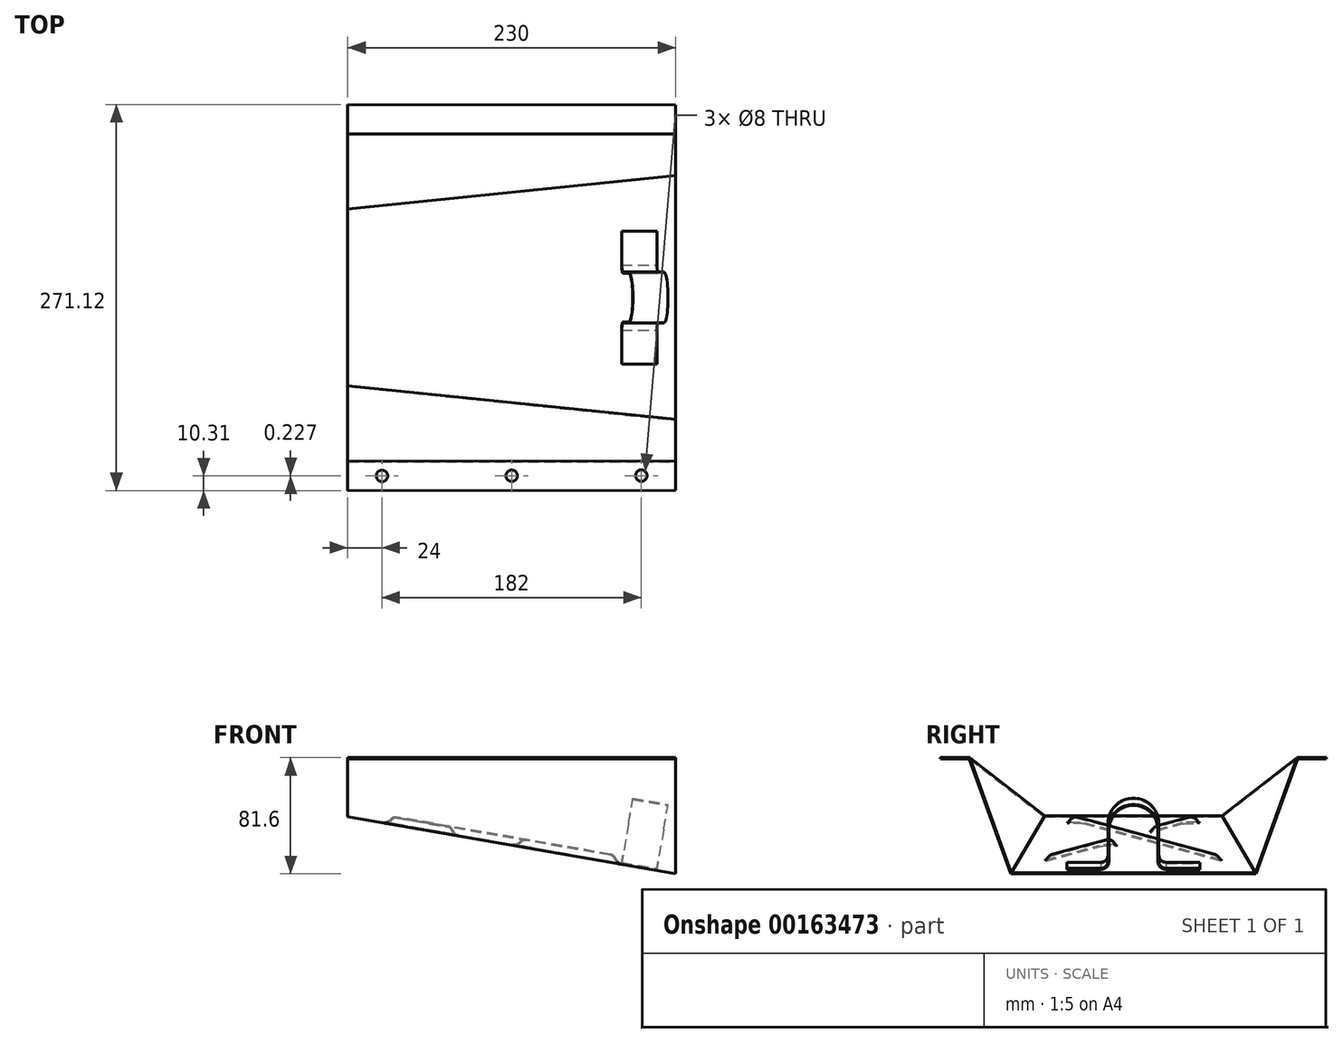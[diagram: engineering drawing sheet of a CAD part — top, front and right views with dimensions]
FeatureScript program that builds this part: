
annotation { "Feature Type Name" : "Feature", "Feature Type Description" : "" }
export const myFeature = defineFeature(function(context is Context, id is Id, definition is map)
    precondition{}
    {
        {
            var Q0;
            Q0=qCreatedBy(makeId("Right.planeOp"),FACE);
            var sketch = newSketch(context, id + "F0", { "sketchPlane" : qUnion([Q0])});
            skLineSegment(sketch, "E0", {"start": v(-135.27, 0) * mm, "end": v(135.27, 0) * mm, "construction": true});
            skLineSegment(sketch, "E1", {"start": v(0, 69.22) * mm, "end": v(0, -69.22) * mm, "construction": true});
            skLineSegment(sketch, "E2", {"start": v(-135.27, 0) * mm, "end": v(-115.27, 0) * mm});
            skLineSegment(sketch, "E3", {"start": v(-115.27, 0) * mm, "end": v(-62.4, -40.8) * mm});
            skLineSegment(sketch, "E4", {"start": v(-62.4, -40.8) * mm, "end": v(0, -40.8) * mm});
            skLineSegment(sketch, "E5.MirrorCS", {"start": v(62.4, -40.8) * mm, "end": v(0, -40.8) * mm});
            skLineSegment(sketch, "E6.MirrorCS", {"start": v(115.27, 0) * mm, "end": v(62.4, -40.8) * mm});
            skLineSegment(sketch, "E7.MirrorCS", {"start": v(135.27, 0) * mm, "end": v(115.27, 0) * mm});
            skLineSegment(sketch, "E8.0", {"start": v(135.56, 0.8) * mm, "end": v(115, 0.8) * mm});
            skLineSegment(sketch, "E8.1", {"start": v(115, 0.8) * mm, "end": v(62.13, -40) * mm});
            skLineSegment(sketch, "E8.2", {"start": v(-135.56, 0.8) * mm, "end": v(-115, 0.8) * mm});
            skLineSegment(sketch, "E8.3", {"start": v(-115, 0.8) * mm, "end": v(-62.13, -40) * mm});
            skLineSegment(sketch, "E8.4", {"start": v(-62.13, -40) * mm, "end": v(0, -40) * mm});
            skLineSegment(sketch, "E8.5", {"start": v(62.13, -40) * mm, "end": v(0, -40) * mm});
            skLineSegment(sketch, "E9", {"start": v(-135.56, 0.8) * mm, "end": v(-135.27, 0) * mm});
            skLineSegment(sketch, "E10", {"start": v(135.56, 0.8) * mm, "end": v(135.27, 0) * mm});
            skSolve(sketch);
        }
        {
            var Q0;
            Q0=qCreatedBy(makeId("Right.planeOp"),FACE);
            cPlane(context, id + "F1", {"entities" : qUnion([Q0]), "cplaneType" : CPlaneType.OFFSET, "offset" : 230 * mm, "width" : 150 * mm, "height" : 150 * mm});
        }
        {
            var Q0;
            Q0=qCreatedBy(id+"F1.planeOp",FACE);
            var sketch = newSketch(context, id + "F2", { "sketchPlane" : qUnion([Q0])});
            skLineSegment(sketch, "E11", {"start": v(-135.27, 0) * mm, "end": v(-115.27, 0) * mm});
            skLineSegment(sketch, "E12", {"start": v(-115.27, 0) * mm, "end": v(-86.15, -80.8) * mm});
            skLineSegment(sketch, "E13", {"start": v(-86.15, -80.8) * mm, "end": v(0, -80.8) * mm});
            skLineSegment(sketch, "E14.MirrorCS", {"start": v(86.15, -80.8) * mm, "end": v(0, -80.8) * mm});
            skLineSegment(sketch, "E15.MirrorCS", {"start": v(115.27, 0) * mm, "end": v(86.15, -80.8) * mm});
            skLineSegment(sketch, "E16.MirrorCS", {"start": v(135.27, 0) * mm, "end": v(115.27, 0) * mm});
            skLineSegment(sketch, "E17.0", {"start": v(135.27, 0.8) * mm, "end": v(114.71, 0.8) * mm});
            skLineSegment(sketch, "E17.1", {"start": v(114.71, 0.8) * mm, "end": v(85.6, -80) * mm});
            skLineSegment(sketch, "E17.2", {"start": v(-135.27, 0.8) * mm, "end": v(-114.71, 0.8) * mm});
            skLineSegment(sketch, "E17.3", {"start": v(-114.71, 0.8) * mm, "end": v(-85.6, -80) * mm});
            skLineSegment(sketch, "E17.4", {"start": v(-85.6, -80) * mm, "end": v(-8.72, -80) * mm});
            skLineSegment(sketch, "E17.5", {"start": v(85.6, -80) * mm, "end": v(-8.72, -80) * mm});
            skLineSegment(sketch, "E18", {"start": v(135.27, 0.8) * mm, "end": v(135.27, 0) * mm});
            skLineSegment(sketch, "E19", {"start": v(-135.27, 0.8) * mm, "end": v(-135.27, 0) * mm});
            skSolve(sketch);
        }
        {
            var Q0;
            Q0=makeQuery(id+"F0.imprint","IMPRINT",FACE,{"disambiguationData":[TD([[makeQuery(id+"F0.imprint","IMPRINT",EDGE,{"derivedFrom":sQuery(id+"F0.wireOp",EDGE,"E2")}),1.0]])]});
            var Q1;
            Q1=makeQuery(id+"F2.imprint","IMPRINT",FACE,{"disambiguationData":[TD([[makeQuery(id+"F2.imprint","IMPRINT",EDGE,{"derivedFrom":sQuery(id+"F2.wireOp",EDGE,"E11")}),1.0]])]});
            loft(context, id + "F3", {"sheetProfilesArray" : [{ "sheetProfileEntities" : qUnion([Q0]) }, { "sheetProfileEntities" : qUnion([Q1]) }]});
        }
        {
            var Q0;
            Q0=makeQuery(id+"F3.opLoft","SWEPT_FACE",FACE,{"disambiguationData":[OSD([sQuery(id+"F0.wireOp",EDGE,"E8.1"),sQuery(id+"F0.wireOp",EDGE,"E8.4"),sQuery(id+"F0.wireOp",EDGE,"E8.5"),sQuery(id+"F2.wireOp",EDGE,"E17.1"),sQuery(id+"F2.wireOp",EDGE,"E17.4"),sQuery(id+"F2.wireOp",EDGE,"E17.5")])]});
            var sketch = newSketch(context, id + "F4", { "sketchPlane" : qUnion([Q0])});
            skLineSegment(sketch, "E20", {"start": v(6.85, -62.13) * mm, "end": v(240.3, 85.6) * mm, "construction": true});
            skLineSegment(sketch, "E21", {"start": v(240.3, -85.6) * mm, "end": v(6.85, 62.13) * mm, "construction": true});
            skArc(sketch, "E22", {"start": v(38.45, -36.22) * mm, "mid": v(36.9, -43.12) * mm, "end": v(43.8, -44.67) * mm});
            skArc(sketch, "E23", {"start": v(195.77, 51.5) * mm, "mid": v(197.32, 58.4) * mm, "end": v(190.42, 59.95) * mm});
            skLineSegment(sketch, "E24", {"start": v(195.77, 51.5) * mm, "end": v(43.8, -44.67) * mm});
            skLineSegment(sketch, "E25", {"start": v(38.45, -36.22) * mm, "end": v(190.42, 59.95) * mm});
            skArc(sketch, "E26", {"start": v(43.8, 44.67) * mm, "mid": v(36.9, 43.12) * mm, "end": v(38.45, 36.22) * mm});
            skArc(sketch, "E27", {"start": v(74.31, 13.53) * mm, "mid": v(81.21, 15.08) * mm, "end": v(79.66, 21.98) * mm});
            skArc(sketch, "E28", {"start": v(190.42, -59.95) * mm, "mid": v(197.32, -58.4) * mm, "end": v(195.77, -51.5) * mm});
            skArc(sketch, "E29", {"start": v(135.76, -13.53) * mm, "mid": v(128.87, -15.08) * mm, "end": v(130.42, -21.98) * mm});
            skLineSegment(sketch, "E30", {"start": v(195.77, -51.5) * mm, "end": v(135.76, -13.53) * mm});
            skLineSegment(sketch, "E31", {"start": v(190.42, -59.95) * mm, "end": v(130.42, -21.98) * mm});
            skLineSegment(sketch, "E32", {"start": v(43.8, 44.67) * mm, "end": v(79.66, 21.98) * mm});
            skLineSegment(sketch, "E33", {"start": v(38.45, 36.22) * mm, "end": v(74.31, 13.53) * mm});
            skLineSegment(sketch, "E34.0", {"start": v(195.34, -52.17) * mm, "end": v(135.34, -14.2) * mm});
            skArc(sketch, "E34.1", {"start": v(190.85, -59.27) * mm, "mid": v(196.65, -57.97) * mm, "end": v(195.34, -52.17) * mm});
            skLineSegment(sketch, "E34.2", {"start": v(190.85, -59.27) * mm, "end": v(130.85, -21.3) * mm});
            skArc(sketch, "E34.3", {"start": v(135.34, -14.2) * mm, "mid": v(129.54, -15.5) * mm, "end": v(130.85, -21.3) * mm});
            skLineSegment(sketch, "E35", {"start": v(226.93, -41.34) * mm, "end": v(226.93, 41.34) * mm, "construction": true});
            skLineSegment(sketch, "E36", {"start": v(168.2, 0) * mm, "end": v(226.93, 0) * mm, "construction": true});
            skSolve(sketch);
        }
        {
            var Q0;
            Q0=makeQuery(id+"F4.imprint","IMPRINT",FACE,{"disambiguationData":[TD([[makeQuery(id+"F4.imprint","IMPRINT",EDGE,{"derivedFrom":sQuery(id+"F4.wireOp",EDGE,"E28")}),1.0]])]});
            var Q1;
            Q1=makeQuery(id+"F4.imprint","IMPRINT",FACE,{"disambiguationData":[TD([[makeQuery(id+"F4.imprint","IMPRINT",EDGE,{"derivedFrom":sQuery(id+"F4.wireOp",EDGE,"E22")}),1.0]])]});
            var Q2;
            Q2=makeQuery(id+"F4.imprint","IMPRINT",FACE,{"disambiguationData":[TD([[makeQuery(id+"F4.imprint","IMPRINT",EDGE,{"derivedFrom":sQuery(id+"F4.wireOp",EDGE,"E26")}),1.0]])]});
            var Q3;
            Q3=makeQuery(id+"F4.imprint","IMPRINT",FACE,{"disambiguationData":[TD([[makeQuery(id+"F4.imprint","IMPRINT",EDGE,{"derivedFrom":sQuery(id+"F4.wireOp",EDGE,"E34.0")}),1.0]])]});
            extrude(context, id + "F5", {"entities" : qUnion([Q0, Q1, Q2, Q3]), "operationType" : NewBodyOperationType.ADD, "depth" : 5 * mm});
        }
        {
            var Q0;
            Q0=makeQuery(id+"F5.opExtrude","CAP_EDGE",EDGE,{"disambiguationData":[OSD([sQuery(id+"F4.wireOp",EDGE,"E30")])],"isStart":false});
            var Q1;
            Q1=makeQuery(id+"F5.opExtrude","CAP_EDGE",EDGE,{"disambiguationData":[OSD([sQuery(id+"F4.wireOp",EDGE,"E24")])],"isStart":false});
            var Q2;
            Q2=makeQuery(id+"F5.opExtrude","CAP_EDGE",EDGE,{"disambiguationData":[OSD([sQuery(id+"F4.wireOp",EDGE,"E27")])],"isStart":false});
            fillet(context, id + "F6", {"entities" : qUnion([Q0, Q1, Q2]), "radius" : 5 * mm, "tangentPropagation" : true, "allowEdgeOverflow" : false});
        }
        {
            var Q0;
            Q0=makeQuery(id+"F3.opLoft","SWEPT_FACE",FACE,{"disambiguationData":[OSD([sQuery(id+"F0.wireOp",EDGE,"E3"),sQuery(id+"F0.wireOp",EDGE,"E4"),sQuery(id+"F0.wireOp",EDGE,"E5.MirrorCS"),sQuery(id+"F2.wireOp",EDGE,"E12"),sQuery(id+"F2.wireOp",EDGE,"E13"),sQuery(id+"F2.wireOp",EDGE,"E14.MirrorCS")])]});
            shell(context, id + "F7", {"entities" : qUnion([Q0]), "thickness" : 0.8 * mm});
        }
        {
            var Q0;
            Q0=sQuery(id+"F4.wireOp",VERTEX,"E36.end");
            var Q1;
            Q1=sQuery(id+"F4.wireOp",EDGE,"E36");
            cPlane(context, id + "F8", {"entities" : qUnion([Q0, Q1]), "cplaneType" : CPlaneType.LINE_POINT, "offset" : 25 * mm, "width" : 150 * mm, "height" : 150 * mm});
        }
        {
            var Q0;
            Q0=qCreatedBy(id+"F8.planeOp",FACE);
            var sketch = newSketch(context, id + "F9", { "sketchPlane" : qUnion([Q0])});
            skArc(sketch, "E37", {"start": v(17.92, -10.95) * mm, "mid": v(0, 6.97) * mm, "end": v(-17.92, -10.95) * mm});
            skLineSegment(sketch, "E38", {"start": v(-17.92, -10.95) * mm, "end": v(-17.92, -33.6) * mm});
            skLineSegment(sketch, "E39", {"start": v(-22.92, -38.6) * mm, "end": v(-46.63, -38.6) * mm});
            skLineSegment(sketch, "E40.MirrorCS", {"start": v(17.92, -10.95) * mm, "end": v(17.92, -33.6) * mm});
            skLineSegment(sketch, "E41.MirrorCS", {"start": v(22.92, -38.6) * mm, "end": v(46.63, -38.6) * mm});
            skPoint(sketch, "E42.visualSharp", {"position": v(-17.92, -38.6) * mm});
            skArc(sketch, "E42.filletArc", {"start": v(-22.92, -38.6) * mm, "mid": v(-19.39, -37.14) * mm, "end": v(-17.92, -33.6) * mm});
            skPoint(sketch, "E43.visualSharp", {"position": v(17.92, -38.6) * mm});
            skArc(sketch, "E43.filletArc", {"start": v(17.92, -33.6) * mm, "mid": v(19.39, -37.14) * mm, "end": v(22.92, -38.6) * mm});
            skLineSegment(sketch, "E44.0", {"start": v(22.92, -39.4) * mm, "end": v(46.63, -39.4) * mm});
            skArc(sketch, "E44.1", {"start": v(17.12, -33.6) * mm, "mid": v(18.82, -37.7) * mm, "end": v(22.92, -39.4) * mm});
            skLineSegment(sketch, "E44.2", {"start": v(17.12, -10.95) * mm, "end": v(17.12, -33.6) * mm});
            skLineSegment(sketch, "E44.3", {"start": v(-22.92, -39.4) * mm, "end": v(-46.63, -39.4) * mm});
            skArc(sketch, "E44.4", {"start": v(-22.92, -39.4) * mm, "mid": v(-18.82, -37.7) * mm, "end": v(-17.12, -33.6) * mm});
            skLineSegment(sketch, "E44.5", {"start": v(-17.12, -10.95) * mm, "end": v(-17.12, -33.6) * mm});
            skArc(sketch, "E44.6", {"start": v(17.12, -10.95) * mm, "mid": v(0, 6.17) * mm, "end": v(-17.12, -10.95) * mm});
            skLineSegment(sketch, "E45", {"start": v(46.63, -38.6) * mm, "end": v(46.63, -39.4) * mm});
            skLineSegment(sketch, "E46", {"start": v(-46.63, -38.6) * mm, "end": v(-46.63, -39.4) * mm});
            skSolve(sketch);
        }
        {
            var Q0;
            Q0=makeQuery(id+"F9.imprint","IMPRINT",FACE,{"disambiguationData":[TD([[makeQuery(id+"F9.imprint","IMPRINT",EDGE,{"derivedFrom":sQuery(id+"F9.wireOp",EDGE,"E37")}),1.0]])]});
            extrude(context, id + "F10", {"entities" : qUnion([Q0]), "operationType" : NewBodyOperationType.ADD, "oppositeDirection" : true, "depth" : 25 * mm});
        }
        {
            var Q0;
            Q0=makeQuery(id+"F6.opFillet","BLEND_EDGE",EDGE,{"blendedFrom":[makeQuery(id+"F5.opExtrude","CAP_EDGE",EDGE,{"disambiguationData":[OSD([sQuery(id+"F4.wireOp",EDGE,"E24")])],"isStart":false}),makeQuery(id+"F3.opLoft","SWEPT_FACE",FACE,{"disambiguationData":[OSD([sQuery(id+"F0.wireOp",EDGE,"E8.1"),sQuery(id+"F0.wireOp",EDGE,"E8.4"),sQuery(id+"F0.wireOp",EDGE,"E8.5"),sQuery(id+"F2.wireOp",EDGE,"E17.1"),sQuery(id+"F2.wireOp",EDGE,"E17.4"),sQuery(id+"F2.wireOp",EDGE,"E17.5")])]})],"blendedInto":[makeQuery(id+"F3.opLoft","SWEPT_FACE",FACE,{"disambiguationData":[OSD([sQuery(id+"F0.wireOp",EDGE,"E8.1"),sQuery(id+"F0.wireOp",EDGE,"E8.4"),sQuery(id+"F0.wireOp",EDGE,"E8.5"),sQuery(id+"F2.wireOp",EDGE,"E17.1"),sQuery(id+"F2.wireOp",EDGE,"E17.4"),sQuery(id+"F2.wireOp",EDGE,"E17.5")])]})]});
            var Q1;
            Q1=makeQuery(id+"F6.opFillet","BLEND_EDGE",EDGE,{"blendedFrom":[makeQuery(id+"F5.opExtrude","CAP_EDGE",EDGE,{"disambiguationData":[OSD([sQuery(id+"F4.wireOp",EDGE,"E33")])],"isStart":false}),makeQuery(id+"F3.opLoft","SWEPT_FACE",FACE,{"disambiguationData":[OSD([sQuery(id+"F0.wireOp",EDGE,"E8.1"),sQuery(id+"F0.wireOp",EDGE,"E8.4"),sQuery(id+"F0.wireOp",EDGE,"E8.5"),sQuery(id+"F2.wireOp",EDGE,"E17.1"),sQuery(id+"F2.wireOp",EDGE,"E17.4"),sQuery(id+"F2.wireOp",EDGE,"E17.5")])]})],"blendedInto":[makeQuery(id+"F3.opLoft","SWEPT_FACE",FACE,{"disambiguationData":[OSD([sQuery(id+"F0.wireOp",EDGE,"E8.1"),sQuery(id+"F0.wireOp",EDGE,"E8.4"),sQuery(id+"F0.wireOp",EDGE,"E8.5"),sQuery(id+"F2.wireOp",EDGE,"E17.1"),sQuery(id+"F2.wireOp",EDGE,"E17.4"),sQuery(id+"F2.wireOp",EDGE,"E17.5")])]})]});
            var Q2;
            Q2=makeQuery(id+"F6.opFillet","BLEND_EDGE",EDGE,{"blendedFrom":[makeQuery(id+"F5.opExtrude","CAP_EDGE",EDGE,{"disambiguationData":[OSD([sQuery(id+"F4.wireOp",EDGE,"E31")])],"isStart":false}),makeQuery(id+"F3.opLoft","SWEPT_FACE",FACE,{"disambiguationData":[OSD([sQuery(id+"F0.wireOp",EDGE,"E8.1"),sQuery(id+"F0.wireOp",EDGE,"E8.4"),sQuery(id+"F0.wireOp",EDGE,"E8.5"),sQuery(id+"F2.wireOp",EDGE,"E17.1"),sQuery(id+"F2.wireOp",EDGE,"E17.4"),sQuery(id+"F2.wireOp",EDGE,"E17.5")])]})],"blendedInto":[makeQuery(id+"F3.opLoft","SWEPT_FACE",FACE,{"disambiguationData":[OSD([sQuery(id+"F0.wireOp",EDGE,"E8.1"),sQuery(id+"F0.wireOp",EDGE,"E8.4"),sQuery(id+"F0.wireOp",EDGE,"E8.5"),sQuery(id+"F2.wireOp",EDGE,"E17.1"),sQuery(id+"F2.wireOp",EDGE,"E17.4"),sQuery(id+"F2.wireOp",EDGE,"E17.5")])]})]});
            var Q3;
            Q3=makeQuery(id+"F7.opShell","TWEAK_EDGE",EDGE,{"disambiguationData":[OD(0.0)],"derivedFrom":[makeQuery(id+"F3.opLoft","SWEPT_FACE",FACE,{"disambiguationData":[OSD([sQuery(id+"F0.wireOp",EDGE,"E3"),sQuery(id+"F0.wireOp",EDGE,"E4"),sQuery(id+"F0.wireOp",EDGE,"E5.MirrorCS"),sQuery(id+"F2.wireOp",EDGE,"E12"),sQuery(id+"F2.wireOp",EDGE,"E13"),sQuery(id+"F2.wireOp",EDGE,"E14.MirrorCS")])]}),makeQuery(id+"F6.opFillet","BLEND_FACE",FACE,{"disambiguationData":[OSD([sQuery(id+"F4.wireOp",EDGE,"E24")])]})]});
            var Q4;
            Q4=makeQuery(id+"F7.opShell","TWEAK_EDGE",EDGE,{"disambiguationData":[OD(1.0)],"derivedFrom":[makeQuery(id+"F3.opLoft","SWEPT_FACE",FACE,{"disambiguationData":[OSD([sQuery(id+"F0.wireOp",EDGE,"E3"),sQuery(id+"F0.wireOp",EDGE,"E4"),sQuery(id+"F0.wireOp",EDGE,"E5.MirrorCS"),sQuery(id+"F2.wireOp",EDGE,"E12"),sQuery(id+"F2.wireOp",EDGE,"E13"),sQuery(id+"F2.wireOp",EDGE,"E14.MirrorCS")])]}),makeQuery(id+"F6.opFillet","BLEND_FACE",FACE,{"disambiguationData":[OSD([sQuery(id+"F4.wireOp",EDGE,"E30")])]})]});
            var Q5;
            Q5=makeQuery(id+"F7.opShell","TWEAK_EDGE",EDGE,{"disambiguationData":[OD(1.0)],"derivedFrom":[makeQuery(id+"F3.opLoft","SWEPT_FACE",FACE,{"disambiguationData":[OSD([sQuery(id+"F0.wireOp",EDGE,"E3"),sQuery(id+"F0.wireOp",EDGE,"E4"),sQuery(id+"F0.wireOp",EDGE,"E5.MirrorCS"),sQuery(id+"F2.wireOp",EDGE,"E12"),sQuery(id+"F2.wireOp",EDGE,"E13"),sQuery(id+"F2.wireOp",EDGE,"E14.MirrorCS")])]}),makeQuery(id+"F6.opFillet","BLEND_FACE",FACE,{"disambiguationData":[OSD([sQuery(id+"F4.wireOp",EDGE,"E32")])]})]});
            fillet(context, id + "F11", {"entities" : qUnion([Q0, Q1, Q2, Q3, Q4, Q5]), "radius" : 5 * mm, "tangentPropagation" : true, "allowEdgeOverflow" : false});
        }
        {
            var Q0;
            Q0=makeQuery(id+"F3.opLoft","SWEPT_FACE",FACE,{"disambiguationData":[OSD([sQuery(id+"F0.wireOp",EDGE,"E8.2"),sQuery(id+"F0.wireOp",EDGE,"E8.3"),sQuery(id+"F0.wireOp",EDGE,"E9"),sQuery(id+"F2.wireOp",EDGE,"E17.2"),sQuery(id+"F2.wireOp",EDGE,"E17.3"),sQuery(id+"F2.wireOp",EDGE,"E19")])]});
            var sketch = newSketch(context, id + "F12", { "sketchPlane" : qUnion([Q0])});
            skLineSegment(sketch, "E47", {"start": v(0, -125.28) * mm, "end": v(230, -125) * mm, "construction": true});
            skLineSegment(sketch, "E48", {"start": v(0, 125.28) * mm, "end": v(230, 125.28) * mm, "construction": true});
            skCircle(sketch, "E49", {"center": v(115, -125.14) * mm, "radius": 4 * mm});
            skCircle(sketch, "E50", {"center": v(24, -125.25) * mm, "radius": 4 * mm});
            skCircle(sketch, "E51", {"center": v(206, -125.02) * mm, "radius": 4 * mm});
            skCircle(sketch, "E52.MirrorC", {"center": v(24, 125.25) * mm, "radius": 4 * mm});
            skCircle(sketch, "E53.MirrorC", {"center": v(115, 125.14) * mm, "radius": 4 * mm});
            skCircle(sketch, "E54.MirrorC", {"center": v(206, 125.02) * mm, "radius": 4 * mm});
            skSolve(sketch);
        }
        {
            var Q0;
            Q0=makeQuery(id+"F12.imprint","IMPRINT",FACE,{"disambiguationData":[TD([[makeQuery(id+"F12.imprint","IMPRINT",EDGE,{"derivedFrom":sQuery(id+"F12.wireOp",EDGE,"E50")}),1.0]])]});
            var Q1;
            Q1=makeQuery(id+"F12.imprint","IMPRINT",FACE,{"disambiguationData":[TD([[makeQuery(id+"F12.imprint","IMPRINT",EDGE,{"derivedFrom":sQuery(id+"F12.wireOp",EDGE,"E49")}),1.0]])]});
            var Q2;
            Q2=makeQuery(id+"F12.imprint","IMPRINT",FACE,{"disambiguationData":[TD([[makeQuery(id+"F12.imprint","IMPRINT",EDGE,{"derivedFrom":sQuery(id+"F12.wireOp",EDGE,"E51")}),1.0]])]});
            var Q3;
            Q3=makeQuery(id+"F12.imprint","IMPRINT",FACE,{"disambiguationData":[TD([[makeQuery(id+"F12.imprint","IMPRINT",EDGE,{"derivedFrom":sQuery(id+"F12.wireOp",EDGE,"E52.MirrorC")}),-1.0]])]});
            var Q4;
            Q4=makeQuery(id+"F12.imprint","IMPRINT",FACE,{"disambiguationData":[TD([[makeQuery(id+"F12.imprint","IMPRINT",EDGE,{"derivedFrom":sQuery(id+"F12.wireOp",EDGE,"E53.MirrorC")}),-1.0]])]});
            var Q5;
            Q5=makeQuery(id+"F12.imprint","IMPRINT",FACE,{"disambiguationData":[TD([[makeQuery(id+"F12.imprint","IMPRINT",EDGE,{"derivedFrom":sQuery(id+"F12.wireOp",EDGE,"E54.MirrorC")}),-1.0]])]});
            extrude(context, id + "F13", {"entities" : qUnion([Q0, Q1, Q2, Q3, Q4, Q5]), "operationType" : NewBodyOperationType.REMOVE, "endBound" : BoundingType.THROUGH_ALL, "oppositeDirection" : true, "depth" : 25 * mm});
        }
    });
